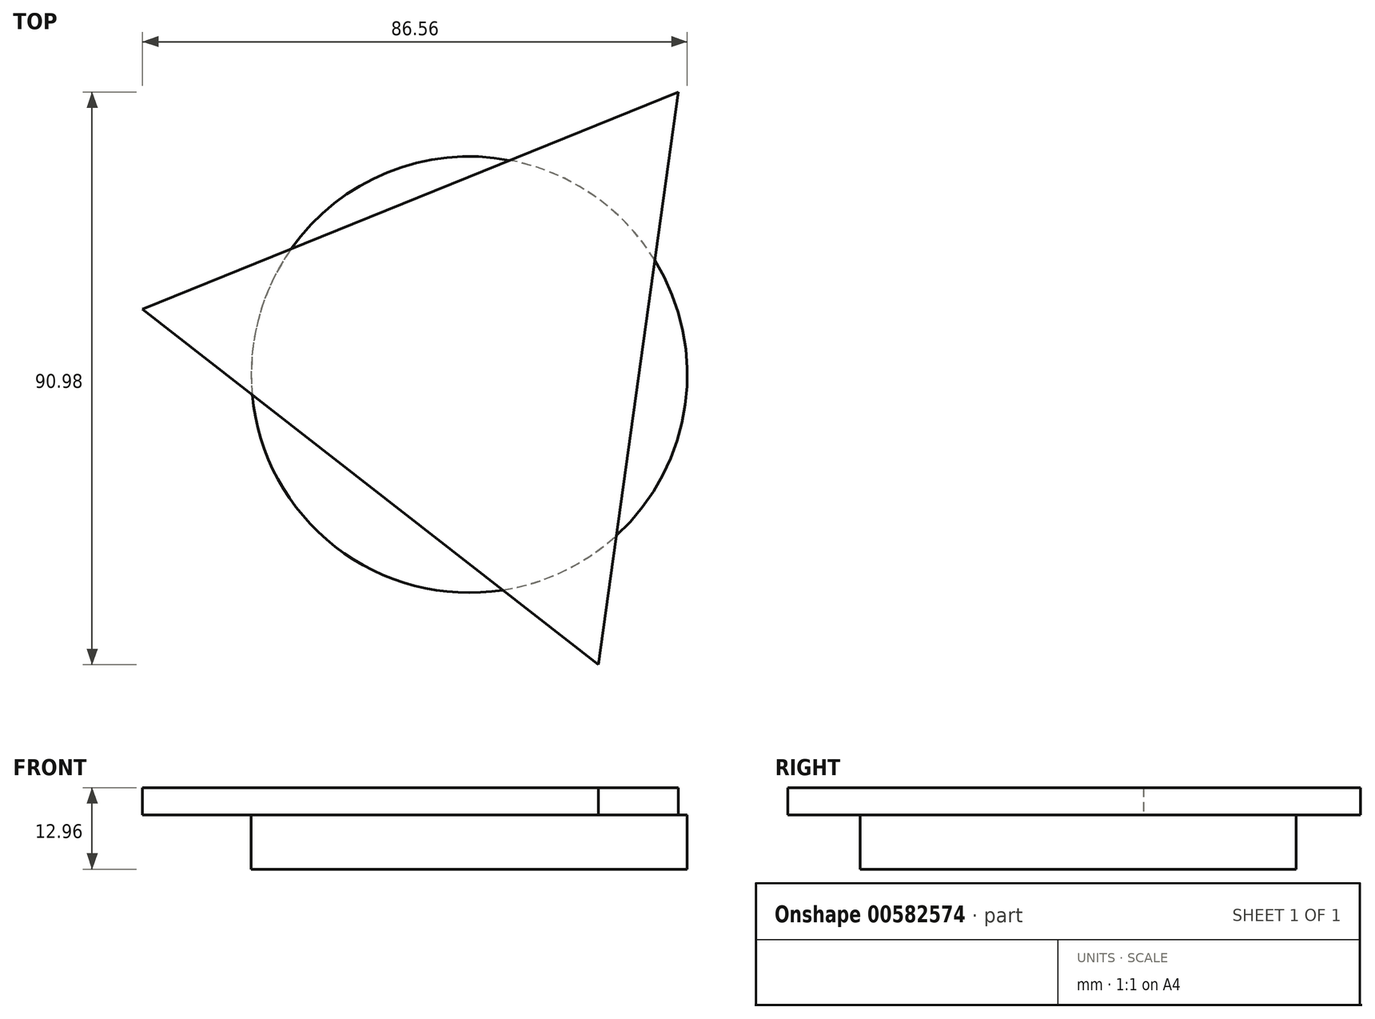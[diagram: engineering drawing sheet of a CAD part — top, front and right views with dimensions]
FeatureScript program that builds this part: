
annotation { "Feature Type Name" : "Feature", "Feature Type Description" : "" }
export const myFeature = defineFeature(function(context is Context, id is Id, definition is map)
    precondition{}
    {
        {
            var Q0;
            Q0=qCreatedBy(makeId("Top.planeOp"),FACE);
            var sketch = newSketch(context, id + "F0", { "sketchPlane" : qUnion([Q0])});
            skCircle(sketch, "E0.cCircle", {"center": v(-39.55, 41.07) * mm, "radius": 26.52 * mm, "construction": true});
            skLineSegment(sketch, "E0.0", {"start": v(-6.94, 82.9) * mm, "end": v(-19.63, -8.08) * mm});
            skLineSegment(sketch, "E0.1", {"start": v(-19.63, -8.08) * mm, "end": v(-92.07, 48.4) * mm});
            skLineSegment(sketch, "E0.2", {"start": v(-92.07, 48.4) * mm, "end": v(-6.94, 82.9) * mm});
            skPoint(sketch, "E0.0.midPoint", {"position": v(-13.28, 37.4) * mm});
            skSolve(sketch);
        }
        {
            var Q0;
            Q0=makeQuery(id+"F0.imprint","IMPRINT",FACE,{"disambiguationData":[TD([[makeQuery(id+"F0.imprint","IMPRINT",EDGE,{"derivedFrom":sQuery(id+"F0.wireOp",EDGE,"E0.0")}),-1.0]])]});
            extrude(context, id + "F1", {"entities" : qUnion([Q0]), "depth" : 4.32 * mm, "offsetDistance" : 25.4 * mm});
        }
        {
            var Q0;
            Q0=makeQuery(id+"F1.opExtrude","CAP_FACE",FACE,{"disambiguationData":[OSD([sQuery(id+"F0.wireOp",EDGE,"E0.0"),sQuery(id+"F0.wireOp",EDGE,"E0.1"),sQuery(id+"F0.wireOp",EDGE,"E0.2")])],"isStart":true});
            var sketch = newSketch(context, id + "F2", { "sketchPlane" : qUnion([Q0])});
            skCircle(sketch, "E1", {"center": v(-40.16, -38.01) * mm, "radius": 34.64 * mm});
            skSolve(sketch);
        }
        {
            var Q0;
            Q0 = qSketchRegion(id + "F2", true);
            extrude(context, id + "F3", {"entities" : qUnion([Q0]), "operationType" : NewBodyOperationType.ADD, "depth" : 8.64 * mm, "offsetDistance" : 25.4 * mm});
        }
    });
